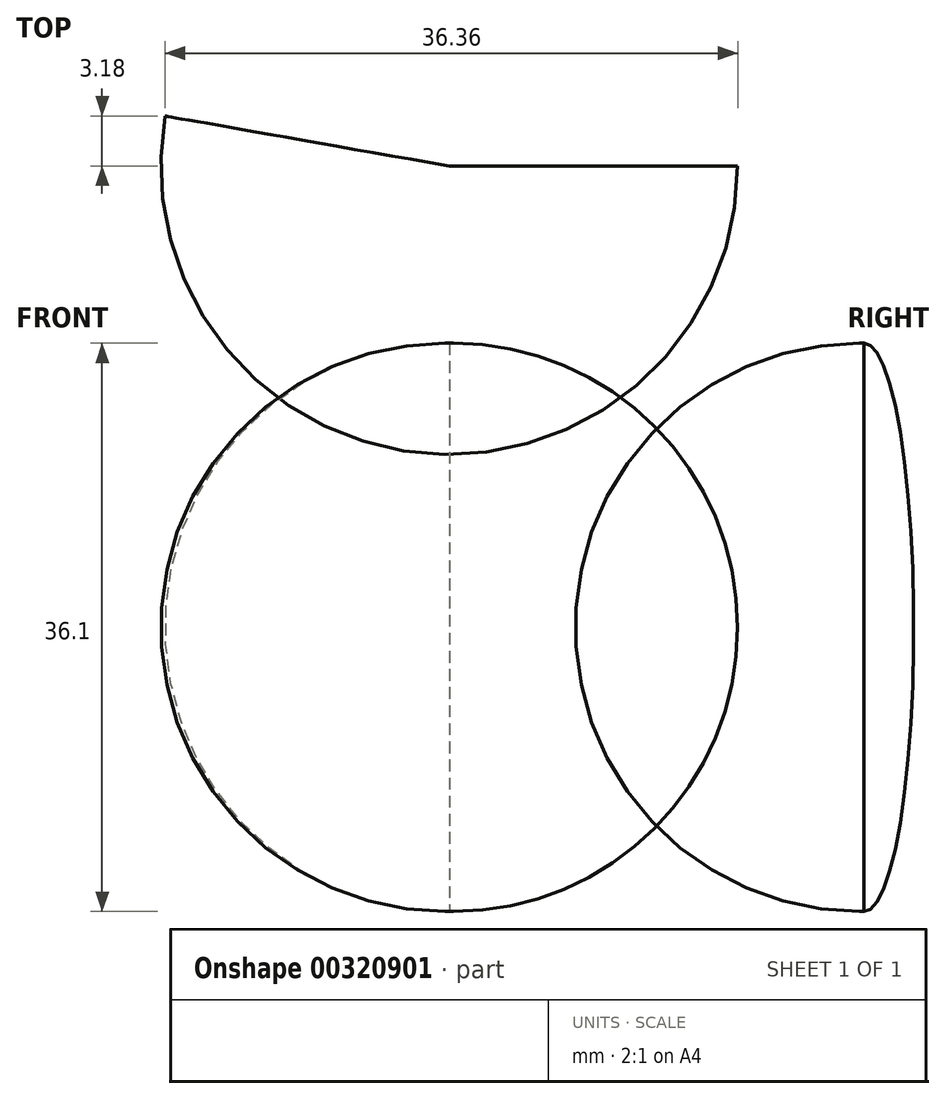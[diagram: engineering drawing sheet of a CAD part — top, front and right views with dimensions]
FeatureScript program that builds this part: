
annotation { "Feature Type Name" : "Feature", "Feature Type Description" : "" }
export const myFeature = defineFeature(function(context is Context, id is Id, definition is map)
    precondition{}
    {
        {
            var Q0;
            Q0=qCreatedBy(makeId("Front.planeOp"),FACE);
            var sketch = newSketch(context, id + "F0", { "sketchPlane" : qUnion([Q0])});
            skLineSegment(sketch, "E0", {"start": v(0, 0) * mm, "end": v(0, -36.1) * mm});
            skArc(sketch, "E1", {"start": v(0, -36.1) * mm, "mid": v(18.32, -18.05) * mm, "end": v(0, 0) * mm});
            skSolve(sketch);
        }
        {
            var Q0;
            Q0 = qSketchRegion(id + "F0", true);
            var Q1;
            Q1=sQuery(id+"F0.wireOp",EDGE,"E0");
            revolve(context, id + "F1", {"entities" : qUnion([Q0]), "axis" : qUnion([Q1]), "revolveType" : RevolveType.ONE_DIRECTION, "angle" : 190 * degree});
        }
        {
            var Q0;
            Q0=makeQuery(id+"F1.opRevolve","CAP_FACE",FACE,{"disambiguationData":[OSD([sQuery(id+"F0.wireOp",EDGE,"E0"),sQuery(id+"F0.wireOp",EDGE,"E1")])],"isStart":true});
            var sketch = newSketch(context, id + "F2", { "sketchPlane" : qUnion([Q0])});
            skArc(sketch, "E2", {"start": v(0, -23.39) * mm, "mid": v(8.33, -15.3) * mm, "end": v(0, -7.2) * mm});
            skSolve(sketch);
        }
        {
            var Q0;
            {var subQ0=makeQuery(id+"F1.opRevolve","CAP_EDGE",EDGE,{"disambiguationData":[OSD([sQuery(id+"F0.wireOp",EDGE,"E1")])],"isStart":true});Q0=makeQuery(id+"F2.imprint","IMPRINT",FACE,{"disambiguationData":[TD([[makeQuery(id+"F2.imprint","IMPRINT",EDGE,{"derivedFrom":subQ0}),-1.0]])]});}
            var Q1;
            Q1=sQuery(id+"F2.wireOp",EDGE,"E2");
            var Q2;
            Q2=makeQuery(id+"F1.opRevolve","CAP_EDGE",EDGE,{"disambiguationData":[OSD([sQuery(id+"F0.wireOp",EDGE,"E0")])],"isStart":true});
            revolve(context, id + "F3", {"bodyType" : ToolBodyType.SURFACE, "entities" : qUnion([Q0]), "surfaceEntities" : qUnion([Q1]), "axis" : qUnion([Q2]), "revolveType" : RevolveType.FULL});
        }
    });
